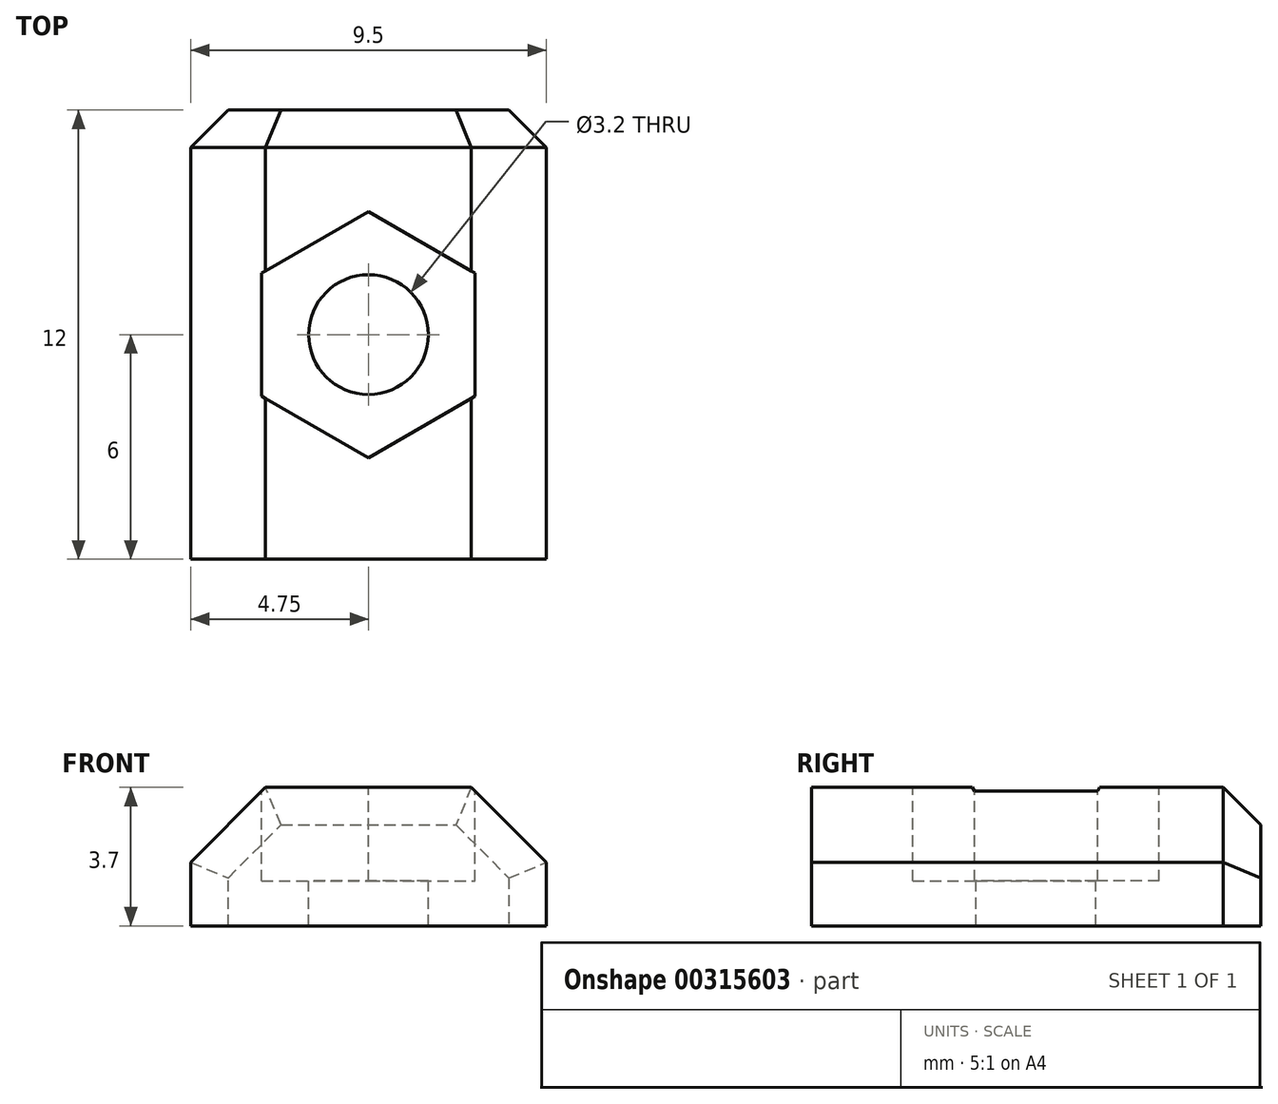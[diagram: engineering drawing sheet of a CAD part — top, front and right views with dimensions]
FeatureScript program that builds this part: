
annotation { "Feature Type Name" : "Feature", "Feature Type Description" : "" }
export const myFeature = defineFeature(function(context is Context, id is Id, definition is map)
    precondition{}
    {
        {
            var Q0;
            Q0=qCreatedBy(makeId("Front.planeOp"),FACE);
            var sketch = newSketch(context, id + "F0", { "sketchPlane" : qUnion([Q0])});
            skLineSegment(sketch, "E0", {"start": v(0, 0) * mm, "end": v(-4.75, 0) * mm});
            skLineSegment(sketch, "E1", {"start": v(0, 0) * mm, "end": v(4.75, 0) * mm});
            skLineSegment(sketch, "E2", {"start": v(4.75, 0) * mm, "end": v(4.75, 3.7) * mm});
            skLineSegment(sketch, "E3", {"start": v(4.75, 3.7) * mm, "end": v(-4.75, 3.7) * mm});
            skLineSegment(sketch, "E4", {"start": v(-4.75, 3.7) * mm, "end": v(-4.75, 0) * mm});
            skSolve(sketch);
        }
        {
            var Q0;
            Q0 = qSketchRegion(id + "F0", true);
            extrude(context, id + "F1", {"entities" : qUnion([Q0]), "endBound" : BoundingType.SYMMETRIC, "depth" : 12 * mm, "offsetDistance" : 25 * mm});
        }
        {
            var Q0;
            Q0=makeQuery(id+"F1.opExtrude","SWEPT_FACE",FACE,{"disambiguationData":[OSD([sQuery(id+"F0.wireOp",EDGE,"E3")])]});
            var sketch = newSketch(context, id + "F2", { "sketchPlane" : qUnion([Q0])});
            skCircle(sketch, "E5", {"center": v(0, 0) * mm, "radius": 1.6 * mm});
            skSolve(sketch);
        }
        {
            var Q0;
            Q0 = qSketchRegion(id + "F2", true);
            extrude(context, id + "F3", {"entities" : qUnion([Q0]), "operationType" : NewBodyOperationType.REMOVE, "endBound" : BoundingType.UP_TO_NEXT, "oppositeDirection" : true, "depth" : 25 * mm});
        }
        {
            var Q0;
            Q0=makeQuery(id+"F1.opExtrude","SWEPT_FACE",FACE,{"disambiguationData":[OSD([sQuery(id+"F0.wireOp",EDGE,"E3")])]});
            var sketch = newSketch(context, id + "F4", { "sketchPlane" : qUnion([Q0])});
            skCircle(sketch, "E6.cCircle", {"center": v(0, 0) * mm, "radius": 2.85 * mm, "construction": true});
            skLineSegment(sketch, "E6.0", {"start": v(2.85, 1.65) * mm, "end": v(2.85, -1.65) * mm});
            skLineSegment(sketch, "E6.1", {"start": v(2.85, -1.65) * mm, "end": v(0, -3.3) * mm});
            skLineSegment(sketch, "E6.2", {"start": v(0, -3.3) * mm, "end": v(-2.85, -1.65) * mm});
            skLineSegment(sketch, "E6.3", {"start": v(-2.85, -1.65) * mm, "end": v(-2.85, 1.65) * mm});
            skLineSegment(sketch, "E6.4", {"start": v(-2.85, 1.65) * mm, "end": v(0, 3.3) * mm});
            skLineSegment(sketch, "E6.5", {"start": v(0, 3.3) * mm, "end": v(2.85, 1.65) * mm});
            skPoint(sketch, "E6.0.midPoint", {"position": v(2.85, 0) * mm});
            skSolve(sketch);
        }
        {
            var Q0;
            Q0=makeQuery(id+"F1.opExtrude","SWEPT_EDGE",EDGE,{"disambiguationData":[OSD([sQuery(id+"F0.wireOp",EDGE,"E3"),sQuery(id+"F0.wireOp",EDGE,"E4")])]});
            var Q1;
            Q1=makeQuery(id+"F1.opExtrude","SWEPT_EDGE",EDGE,{"disambiguationData":[OSD([sQuery(id+"F0.wireOp",EDGE,"E2"),sQuery(id+"F0.wireOp",EDGE,"E3")])]});
            chamfer(context, id + "F5", {"entities" : qUnion([Q0, Q1]), "chamferType" : ChamferType.TWO_OFFSETS, "width1" : 2 * mm, "oppositeDirection" : false, "width2" : 2 * mm, "tangentPropagation" : true});
        }
        {
            var Q0;
            Q0 = qSketchRegion(id + "F4", true);
            extrude(context, id + "F6", {"entities" : qUnion([Q0]), "operationType" : NewBodyOperationType.REMOVE, "oppositeDirection" : true, "depth" : 2.5 * mm});
        }
        {
            var Q0;
            {var subQ0=sQuery(id+"F0.wireOp",EDGE,"E3");var subQ1=sQuery(id+"F0.wireOp",EDGE,"E2");Q0=makeQuery(id+"F5.opChamfer","BLEND_EDGE",EDGE,{"blendedFrom":[makeQuery(id+"F1.opExtrude","SWEPT_EDGE",EDGE,{"disambiguationData":[OSD([subQ1,subQ0])]}),makeQuery(id+"F1.opExtrude","CAP_FACE",FACE,{"disambiguationData":[OSD([sQuery(id+"F0.wireOp",EDGE,"E0"),sQuery(id+"F0.wireOp",EDGE,"E1"),subQ1,subQ0,sQuery(id+"F0.wireOp",EDGE,"E4")])],"isStart":true})],"blendedInto":[makeQuery(id+"F1.opExtrude","CAP_FACE",FACE,{"disambiguationData":[OSD([sQuery(id+"F0.wireOp",EDGE,"E0"),sQuery(id+"F0.wireOp",EDGE,"E1"),subQ1,subQ0,sQuery(id+"F0.wireOp",EDGE,"E4")])],"isStart":true})]});}
            var Q1;
            {var subQ0=sQuery(id+"F0.wireOp",EDGE,"E4");var subQ1=sQuery(id+"F0.wireOp",EDGE,"E3");Q1=makeQuery(id+"F5.opChamfer","BLEND_EDGE",EDGE,{"blendedFrom":[makeQuery(id+"F1.opExtrude","SWEPT_EDGE",EDGE,{"disambiguationData":[OSD([subQ1,subQ0])]}),makeQuery(id+"F1.opExtrude","CAP_FACE",FACE,{"disambiguationData":[OSD([sQuery(id+"F0.wireOp",EDGE,"E0"),sQuery(id+"F0.wireOp",EDGE,"E1"),sQuery(id+"F0.wireOp",EDGE,"E2"),subQ1,subQ0])],"isStart":true})],"blendedInto":[makeQuery(id+"F1.opExtrude","CAP_FACE",FACE,{"disambiguationData":[OSD([sQuery(id+"F0.wireOp",EDGE,"E0"),sQuery(id+"F0.wireOp",EDGE,"E1"),sQuery(id+"F0.wireOp",EDGE,"E2"),subQ1,subQ0])],"isStart":true})]});}
            var Q2;
            Q2=makeQuery(id+"F1.opExtrude","CAP_EDGE",EDGE,{"disambiguationData":[OSD([sQuery(id+"F0.wireOp",EDGE,"E4")])],"isStart":true});
            var Q3;
            Q3=makeQuery(id+"F1.opExtrude","CAP_EDGE",EDGE,{"disambiguationData":[OSD([sQuery(id+"F0.wireOp",EDGE,"E2")])],"isStart":true});
            var Q4;
            Q4=makeQuery(id+"F1.opExtrude","CAP_EDGE",EDGE,{"disambiguationData":[OSD([sQuery(id+"F0.wireOp",EDGE,"E3")])],"isStart":true});
            chamfer(context, id + "F7", {"entities" : qUnion([Q0, Q1, Q2, Q3, Q4]), "width" : 1 * mm, "tangentPropagation" : true});
        }
    });
